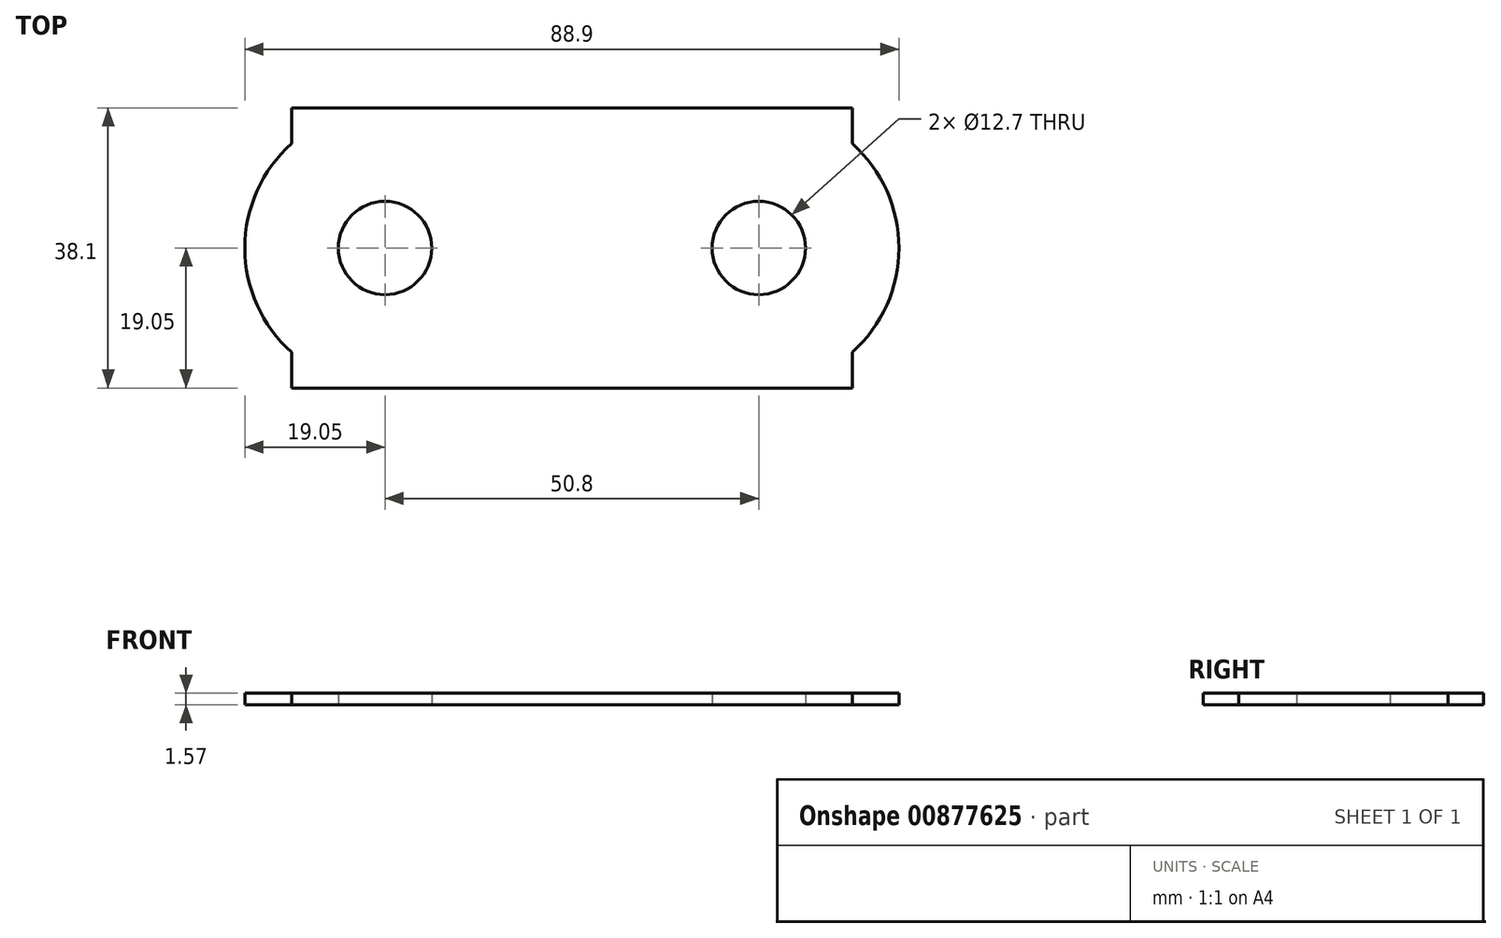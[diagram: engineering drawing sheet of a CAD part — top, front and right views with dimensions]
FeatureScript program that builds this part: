
annotation { "Feature Type Name" : "Feature", "Feature Type Description" : "" }
export const myFeature = defineFeature(function(context is Context, id is Id, definition is map)
    precondition{}
    {
        {
            var Q0;
            Q0=qCreatedBy(makeId("Top.planeOp"),FACE);
            var sketch = newSketch(context, id + "F0", { "sketchPlane" : qUnion([Q0])});
            skLineSegment(sketch, "E0.bottom", {"start": v(-38.1, 19.05) * mm, "end": v(38.1, 19.05) * mm});
            skCircle(sketch, "E1", {"center": v(-25.4, 0) * mm, "radius": 6.35 * mm});
            skArc(sketch, "E2", {"start": v(-38.1, 14.2) * mm, "mid": v(-44.45, 0) * mm, "end": v(-38.1, -14.2) * mm});
            skLineSegment(sketch, "E3.trimOffspring", {"start": v(-38.1, -14.2) * mm, "end": v(-38.1, -19.05) * mm});
            skArc(sketch, "E4.MirrorCS", {"start": v(38.1, 14.2) * mm, "mid": v(44.45, 0) * mm, "end": v(38.1, -14.2) * mm});
            skCircle(sketch, "E5.MirrorC", {"center": v(25.4, 0) * mm, "radius": 6.35 * mm});
            skLineSegment(sketch, "E6.MirrorCS", {"start": v(38.1, -14.2) * mm, "end": v(38.1, -19.05) * mm});
            skLineSegment(sketch, "E7", {"start": v(-38.1, -19.05) * mm, "end": v(38.1, -19.05) * mm});
            skLineSegment(sketch, "E8", {"start": v(-38.1, 19.05) * mm, "end": v(-38.1, 14.2) * mm});
            skLineSegment(sketch, "E9", {"start": v(38.1, 19.05) * mm, "end": v(38.1, 14.2) * mm});
            skSolve(sketch);
        }
        {
            var Q0;
            Q0=makeQuery(id+"F0.imprint","IMPRINT",FACE,{"disambiguationData":[TD([[makeQuery(id+"F0.imprint","IMPRINT",EDGE,{"derivedFrom":sQuery(id+"F0.wireOp",EDGE,"E0.bottom")}),-1.0]])]});
            extrude(context, id + "F1", {"entities" : qUnion([Q0]), "depth" : 1.57 * mm, "offsetDistance" : 25.4 * mm});
        }
    });
